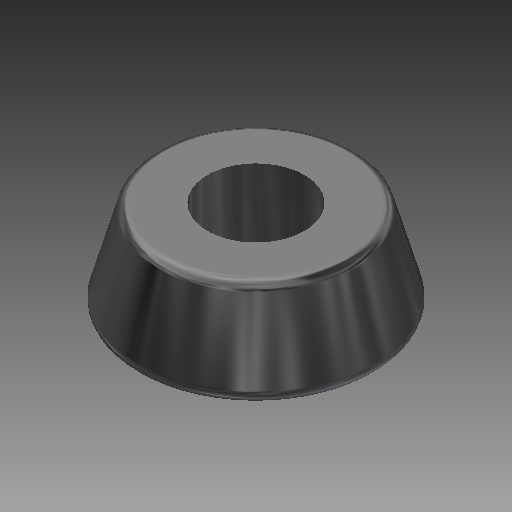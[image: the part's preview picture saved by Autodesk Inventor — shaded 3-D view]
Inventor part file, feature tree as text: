
AUTODESK INVENTOR PART (.ipt)
format: ipt  version: 2019 (Build 230136000, 136)  size: 155,648 bytes
history: native  units: mm
features: revolve x1, fillet x1
ambient origin geometry x8: Origin, YZ Plane, XZ Plane, XY Plane, X Axis, Y Axis, Z Axis, Center Point
bodies: Body1 (feature_tree)
feature tree (2):
  revolve  "Rivoluzione2"
  fillet  "Raccordo2"  [1 undecoded]
note: 1 required parameter value undecoded (feature->parameter linkage not recoverable at this tier; creation-order binding heuristic only, values carry confidence <= 0.55)
